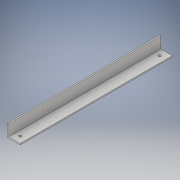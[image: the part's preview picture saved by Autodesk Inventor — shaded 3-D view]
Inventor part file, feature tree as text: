
AUTODESK INVENTOR PART (.ipt)
format: ipt  version: 2017 (Build 210142000, 142)  size: 109,568 bytes
history: native  units: in
note: dims shown in document units (in); Inventor stores cm internally (conversion verified against a paired STEP export)
features: sketch x2, extrude x1, hole x1
ambient origin geometry x8: Origin, YZ Plane, XZ Plane, XY Plane, X Axis, Y Axis, Z Axis, Center Point
bodies: Solid1 (feature_tree)
feature tree (4):
  extrude  "Extrusion1"  Depth=1.0in
  hole  "Hole1"  [1 undecoded]
  sketch  "Sketch1"  dims[d0=1.0in d1=1.0in]
  sketch  "Sketch2"  dims[d2=0.1in d3=12.0in d4=0.0in d5=0.5in d6=0.5in d7=0.7874in d9=11.0in d10=0.3937in d12=1.0in d14=0.201in d15=0.75in d16=0.385in d17=0.25in d18=0.5635in d19=1.0in d20=0.8108in]
note: 1 required parameter value undecoded (feature->parameter linkage not recoverable at this tier; creation-order binding heuristic only, values carry confidence <= 0.55)
